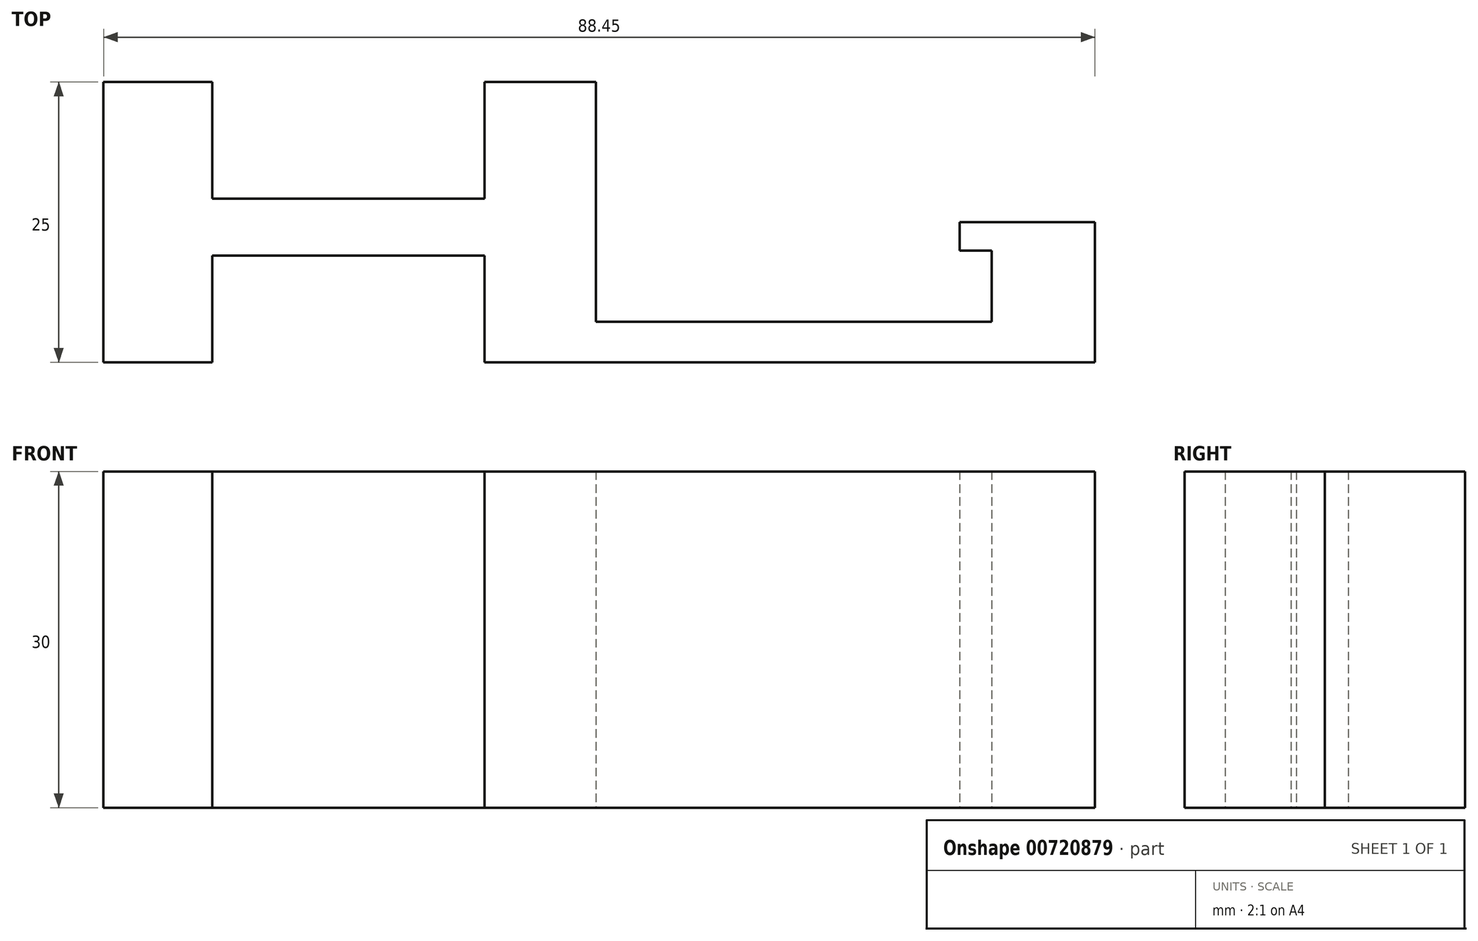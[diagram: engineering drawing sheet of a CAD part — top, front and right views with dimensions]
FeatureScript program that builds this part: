
annotation { "Feature Type Name" : "Feature", "Feature Type Description" : "" }
export const myFeature = defineFeature(function(context is Context, id is Id, definition is map)
    precondition{}
    {
        {
            var Q0;
            Q0=qCreatedBy(makeId("Top.planeOp"),FACE);
            var sketch = newSketch(context, id + "F0", { "sketchPlane" : qUnion([Q0])});
            skLineSegment(sketch, "E0.bottom", {"start": v(-18.67, 0) * mm, "end": v(-28.37, 0) * mm});
            skLineSegment(sketch, "E0.top", {"start": v(-18.67, -25) * mm, "end": v(-28.37, -25) * mm});
            skLineSegment(sketch, "E0.left", {"start": v(-18.67, 0) * mm, "end": v(-18.67, -25) * mm});
            skLineSegment(sketch, "E0.right", {"start": v(-28.37, 0) * mm, "end": v(-28.37, -25) * mm});
            skLineSegment(sketch, "E1.bottom", {"start": v(5.6, 0) * mm, "end": v(15.56, 0) * mm});
            skLineSegment(sketch, "E1.top", {"start": v(5.6, -25) * mm, "end": v(15.56, -25) * mm});
            skLineSegment(sketch, "E1.left", {"start": v(5.6, 0) * mm, "end": v(5.6, -25) * mm});
            skLineSegment(sketch, "E1.right", {"start": v(15.56, 0) * mm, "end": v(15.56, -25) * mm});
            skLineSegment(sketch, "E2", {"start": v(50.86, -25) * mm, "end": v(15.56, -25) * mm});
            skLineSegment(sketch, "E3", {"start": v(15.56, -21.4) * mm, "end": v(50.92, -21.4) * mm});
            skLineSegment(sketch, "E4.bottom", {"start": v(50.86, -25) * mm, "end": v(60.08, -25) * mm});
            skLineSegment(sketch, "E4.top", {"start": v(50.86, -12.5) * mm, "end": v(60.08, -12.5) * mm});
            skLineSegment(sketch, "E4.left", {"start": v(50.86, -25) * mm, "end": v(50.86, -12.5) * mm});
            skLineSegment(sketch, "E4.right", {"start": v(60.08, -25) * mm, "end": v(60.08, -12.5) * mm});
            skLineSegment(sketch, "E5", {"start": v(50.86, -12.5) * mm, "end": v(48.01, -12.5) * mm});
            skLineSegment(sketch, "E6", {"start": v(48.01, -12.5) * mm, "end": v(48.01, -15.04) * mm});
            skLineSegment(sketch, "E7", {"start": v(48.01, -15.04) * mm, "end": v(50.86, -15.04) * mm});
            skLineSegment(sketch, "E8", {"start": v(-18.67, -10.41) * mm, "end": v(5.6, -10.41) * mm});
            skLineSegment(sketch, "E9", {"start": v(-18.67, -15.5) * mm, "end": v(5.6, -15.5) * mm});
            skSolve(sketch);
        }
        {
            var Q0;
            Q0 = qSketchRegion(id + "F0", true);
            extrude(context, id + "F1", {"entities" : qUnion([Q0]), "depth" : 30 * mm, "offsetDistance" : 25 * mm});
        }
    });
